# Revit family: Indoor_Pendant Lamp_Santa&Cole_Sistema Sisisí GT2
name_source: partatom
category: Luminarias
revit_build: Autodesk Revit 2018 (Build: 20190510_1515(x64)
units: mm (PartAtom-declared; Revit-internal decimal feet)

## family parameters
Anfitrión = Cara
Compartido = No
Corte con vacíos al cargar = No
Cota de conector redondo = Diámetro de uso
Origen de luz = Sí
Punto de cálculo de habitación = No
Tipo de pieza = Normal

## types (7) — shared parameters
Archivo de red fotométrica = SISxx+PPT11.IES
Assembly Instructions - CE = https://www.santacole.com
Cambio de temperatura de color de luz atenuada = <Ninguno>
Carga aparente = 12 W
Code = SISxx/SISDx+PGT2x
Elevación por defecto = 1219 mm
Fabricante = Santa & Cole
Filtro de color = 16777215
Load = 12 W
Manufacturer website = http://www.santacole.com
Modelo = Sistema Sisisí
Technical Information = https://www.santacole.com
URL = https://www.santacole.com
Voltaje (90-305 V) = 220 V
Ángulo de inclinación = -90.00°

## per-type parameters (varying)
| type | Lampshade Material | Visibility_Beige Parchment |
| Stitched Beige Cardboard | Santa & Cole - Beige Cardboard | Sí |
| Natural Ribbon | Santa & Cole - Natural Ribbon | No |
| Red-amber Ribbon | Santa & Cole - Red-amber Ribbon | No |
| Black Ribbon | Santa & Cole - Black Ribbon | No |
| Terracota Raw Color Ribbon | Santa & Cole - Terracota Raw Color Ribbon | No |
| Mustard Raw Color Ribbon | Santa & Cole - Mustard Raw Color Ribbon | No |
| Green Raw Color Ribbon | Santa & Cole - Green Raw Color Ribbon | No |

## geometry (parser evidence)
native form markers: Sweep x2
no freeform markers — native parametric forms only
